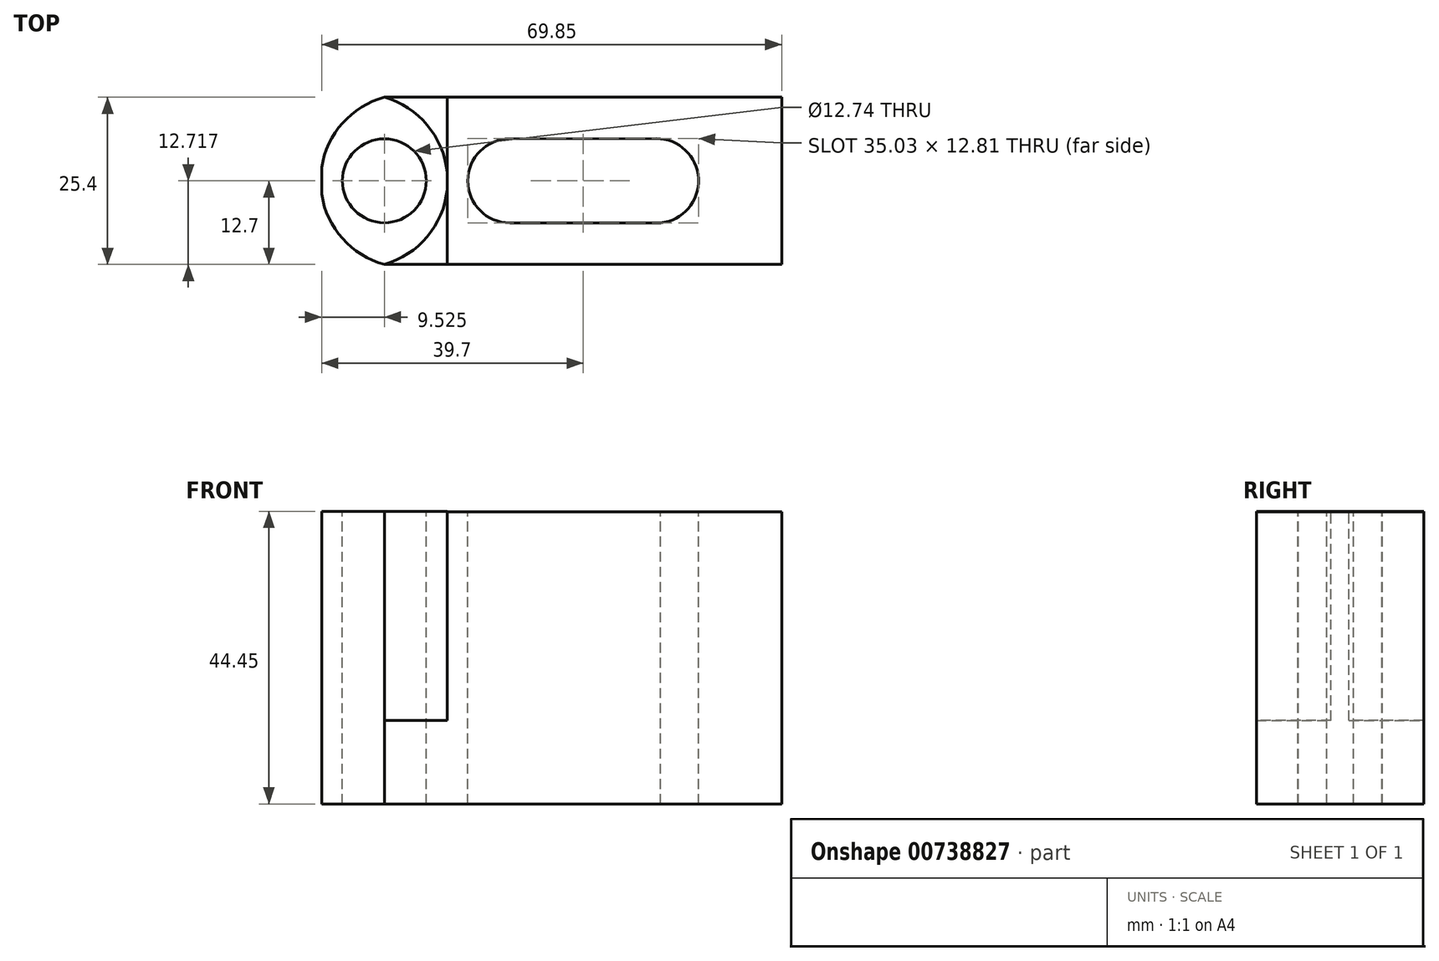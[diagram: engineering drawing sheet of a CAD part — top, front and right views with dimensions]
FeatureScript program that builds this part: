
annotation { "Feature Type Name" : "Feature", "Feature Type Description" : "" }
export const myFeature = defineFeature(function(context is Context, id is Id, definition is map)
    precondition{}
    {
        {
            var Q0;
            Q0=qCreatedBy(makeId("Front.planeOp"),FACE);
            var sketch = newSketch(context, id + "F0", { "sketchPlane" : qUnion([Q0])});
            skLineSegment(sketch, "E0", {"start": v(0, 0) * mm, "end": v(0, 44.45) * mm});
            skLineSegment(sketch, "E1", {"start": v(0, 44.45) * mm, "end": v(69.85, 44.45) * mm});
            skLineSegment(sketch, "E2", {"start": v(69.85, 44.45) * mm, "end": v(69.85, 0) * mm});
            skLineSegment(sketch, "E3", {"start": v(69.85, 0) * mm, "end": v(0, 0) * mm});
            skSolve(sketch);
        }
        {
            var Q0;
            Q0 = qSketchRegion(id + "F0", true);
            extrude(context, id + "F1", {"entities" : qUnion([Q0]), "depth" : 25.4 * mm, "offsetDistance" : 25.4 * mm});
        }
        {
            var Q0;
            Q0=makeQuery(id+"F1.opExtrude","SWEPT_FACE",FACE,{"disambiguationData":[OSD([sQuery(id+"F0.wireOp",EDGE,"E1")])]});
            var sketch = newSketch(context, id + "F2", { "sketchPlane" : qUnion([Q0])});
            skLineSegment(sketch, "E4", {"start": v(19.05, 0) * mm, "end": v(19.05, -25.4) * mm});
            skSolve(sketch);
        }
        {
            var Q0;
            {var subQ0=sQuery(id+"F2.wireOp",EDGE,"E4");Q0=makeQuery(id+"F2.imprint","IMPRINT",FACE,{"disambiguationData":[TD([[makeQuery(id+"F2.imprint","IMPRINT",EDGE,{"derivedFrom":subQ0}),1.0]])]});}
            extrude(context, id + "F3", {"entities" : qUnion([Q0]), "operationType" : NewBodyOperationType.REMOVE, "oppositeDirection" : true, "depth" : 5 / 101.6 * mm, "offsetDistance" : 25.4 * mm});
        }
        {
            var Q0;
            Q0=makeQuery(id+"F1.opExtrude","SWEPT_FACE",FACE,{"disambiguationData":[OSD([sQuery(id+"F0.wireOp",EDGE,"E1")])]});
            var sketch = newSketch(context, id + "F4", { "sketchPlane" : qUnion([Q0])});
            skLineSegment(sketch, "E5", {"start": v(9.53, 0) * mm, "end": v(9.53, -25.4) * mm});
            skCircle(sketch, "E6", {"center": v(9.53, -12.7) * mm, "radius": 6.37 * mm});
            skArc(sketch, "E7", {"start": v(9.53, -25.4) * mm, "mid": v(19.15, -12.7) * mm, "end": v(9.53, 0) * mm});
            skArc(sketch, "E8", {"start": v(9.53, 0) * mm, "mid": v(-0.16, -12.7) * mm, "end": v(9.53, -25.4) * mm});
            skSolve(sketch);
        }
        {
            var Q0;
            {var subQ0=sQuery(id+"F4.wireOp",EDGE,"E6");var subQ1=sQuery(id+"F4.wireOp",EDGE,"E5");var subQ2=makeQuery(id+"F4.imprint","INTERSECT",VERTEX,{"disambiguationData":[OD(0.0)],"derivedFrom":[subQ1,subQ0]});Q0=makeQuery(id+"F4.imprint","IMPRINT",FACE,{"disambiguationData":[TD([[makeQuery(id+"F4.imprint","IMPRINT",EDGE,{"disambiguationData":[TD([[subQ2,-1.0]])],"derivedFrom":subQ1}),-1.0]])]});}
            var Q1;
            {var subQ0=sQuery(id+"F4.wireOp",EDGE,"E6");var subQ1=sQuery(id+"F4.wireOp",EDGE,"E5");var subQ2=makeQuery(id+"F4.imprint","INTERSECT",VERTEX,{"disambiguationData":[OD(0.0)],"derivedFrom":[subQ1,subQ0]});Q1=makeQuery(id+"F4.imprint","IMPRINT",FACE,{"disambiguationData":[TD([[makeQuery(id+"F4.imprint","IMPRINT",EDGE,{"disambiguationData":[TD([[subQ2,-1.0]])],"derivedFrom":subQ1}),1.0]])]});}
            var Q2;
            {var subQ0=sQuery(id+"F4.wireOp",EDGE,"E8");var subQ1=sQuery(id+"F0.wireOp",EDGE,"E1");var subQ4=makeQuery(id+"F1.opExtrude","SWEPT_EDGE",EDGE,{"disambiguationData":[OSD([sQuery(id+"F0.wireOp",EDGE,"E0"),subQ1])]});var subQ5=makeQuery(id+"F4.imprint","INTERSECT",VERTEX,{"disambiguationData":[OD(0.0)],"derivedFrom":[subQ4,subQ0]});Q2=makeQuery(id+"F4.imprint","IMPRINT",FACE,{"disambiguationData":[TD([[makeQuery(id+"F4.imprint","IMPRINT",EDGE,{"disambiguationData":[TD([[subQ5,1.0]])],"derivedFrom":subQ0}),-1.0]])]});}
            var Q3;
            {var subQ0=sQuery(id+"F4.wireOp",EDGE,"E8");var subQ1=sQuery(id+"F0.wireOp",EDGE,"E1");var subQ4=makeQuery(id+"F1.opExtrude","SWEPT_EDGE",EDGE,{"disambiguationData":[OSD([sQuery(id+"F0.wireOp",EDGE,"E0"),subQ1])]});var subQ5=makeQuery(id+"F4.imprint","INTERSECT",VERTEX,{"disambiguationData":[OD(1.0)],"derivedFrom":[subQ4,subQ0]});Q3=makeQuery(id+"F4.imprint","IMPRINT",FACE,{"disambiguationData":[TD([[makeQuery(id+"F4.imprint","IMPRINT",EDGE,{"disambiguationData":[TD([[subQ5,-1.0]])],"derivedFrom":subQ0}),-1.0]])]});}
            extrude(context, id + "F5", {"entities" : qUnion([Q0, Q1, Q2, Q3]), "operationType" : NewBodyOperationType.REMOVE, "endBound" : BoundingType.THROUGH_ALL, "oppositeDirection" : true, "depth" : 25.4 * mm, "offsetDistance" : 25.4 * mm});
        }
        {
            var Q0;
            Q0=makeQuery(id+"F1.opExtrude","SWEPT_FACE",FACE,{"disambiguationData":[OSD([sQuery(id+"F0.wireOp",EDGE,"E1")])]});
            var sketch = newSketch(context, id + "F6", { "sketchPlane" : qUnion([Q0])});
            skArc(sketch, "E9", {"start": v(9.53, -25.4) * mm, "mid": v(19.12, -12.7) * mm, "end": v(9.53, 0) * mm});
            skSolve(sketch);
        }
        {
            var Q0;
            {var subQ1=sQuery(id+"F0.wireOp",EDGE,"E1");var subQ2=makeQuery(id+"F1.opExtrude","CAP_EDGE",EDGE,{"disambiguationData":[OSD([subQ1])],"isStart":true});var subQ3=subQ2;Q0=makeQuery(id+"F6.imprint","IMPRINT",FACE,{"disambiguationData":[TD([[makeQuery(id+"F6.imprint","IMPRINT",EDGE,{"derivedFrom":subQ3}),-1.0]])]});}
            var Q1;
            {var subQ1=sQuery(id+"F0.wireOp",EDGE,"E1");var subQ2=makeQuery(id+"F1.opExtrude","CAP_EDGE",EDGE,{"disambiguationData":[OSD([subQ1])],"isStart":false});var subQ3=subQ2;Q1=makeQuery(id+"F6.imprint","IMPRINT",FACE,{"disambiguationData":[TD([[makeQuery(id+"F6.imprint","IMPRINT",EDGE,{"derivedFrom":subQ3}),1.0]])]});}
            extrude(context, id + "F7", {"entities" : qUnion([Q0, Q1]), "operationType" : NewBodyOperationType.REMOVE, "oppositeDirection" : true, "depth" : 31.75 * mm, "offsetDistance" : 25.4 * mm});
        }
        {
            var Q0;
            {var subQ0=sQuery(id+"F0.wireOp",EDGE,"E1");var subQ1=makeQuery(id+"F1.opExtrude","CAP_EDGE",EDGE,{"disambiguationData":[OSD([subQ0])],"isStart":true});var subQ2=subQ1;var subQ3=sQuery(id+"F2.wireOp",EDGE,"E4");var subQ4=makeQuery(id+"F3.boolean.opBoolean","COPY",EDGE,{"derivedFrom":makeQuery(id+"F3.opExtrude","CAP_EDGE",EDGE,{"disambiguationData":[OSD([subQ3])],"isStart":true})});var subQ5=sQuery(id+"F6.wireOp",EDGE,"E9");var subQ6=makeQuery(id+"F6.imprint","INTERSECT",VERTEX,{"disambiguationData":[OD(1.0)],"derivedFrom":[subQ4,subQ5]});var subQ11=makeQuery(id+"F1.opExtrude","CAP_EDGE",EDGE,{"disambiguationData":[OSD([subQ0])],"isStart":false});var subQ12=subQ11;var subQ13=makeQuery(id+"F6.imprint","INTERSECT",VERTEX,{"disambiguationData":[OD(0.0)],"derivedFrom":[subQ4,subQ5]});Q0=makeQuery(id+"F7.boolean.opBoolean","MERGE",FACE,{"derivedFrom":[makeQuery(id+"F3.boolean.opBoolean","COPY",FACE,{"derivedFrom":makeQuery(id+"F3.opExtrude","CAP_FACE",FACE,{"disambiguationData":[OSD([subQ0,sQuery(id+"F0.wireOp",EDGE,"E2"),subQ3])],"isStart":false})}),makeQuery(id+"F7.opExtrude","CAP_FACE",FACE,{"disambiguationData":[OSD([subQ0,subQ3,subQ5]),TDD([makeQuery(id+"F6.imprint","IMPRINT",EDGE,{"disambiguationData":[TD([[subQ13,1.0]])],"derivedFrom":subQ5}),makeQuery(id+"F6.imprint","IMPRINT",EDGE,{"derivedFrom":subQ12}),makeQuery(id+"F6.imprint","IMPRINT",EDGE,{"disambiguationData":[TD([[makeQuery(id+"F6.imprint","INTERSECT",VERTEX,{"derivedFrom":[subQ4,subQ12]}),1.0]])],"derivedFrom":subQ4})])],"isStart":false}),makeQuery(id+"F7.opExtrude","CAP_FACE",FACE,{"disambiguationData":[OSD([subQ0,subQ3,subQ5]),TDD([makeQuery(id+"F6.imprint","IMPRINT",EDGE,{"disambiguationData":[TD([[subQ6,-1.0]])],"derivedFrom":subQ5}),makeQuery(id+"F6.imprint","IMPRINT",EDGE,{"derivedFrom":subQ2}),makeQuery(id+"F6.imprint","IMPRINT",EDGE,{"disambiguationData":[TD([[makeQuery(id+"F6.imprint","INTERSECT",VERTEX,{"derivedFrom":[subQ4,subQ2]}),-1.0]])],"derivedFrom":subQ4})])],"isStart":false})]});}
            var sketch = newSketch(context, id + "F8", { "sketchPlane" : qUnion([Q0])});
            skLineSegment(sketch, "E10", {"start": v(28.58, 0) * mm, "end": v(28.58, -25.4) * mm});
            skLineSegment(sketch, "E11", {"start": v(50.8, 0) * mm, "end": v(50.8, -25.4) * mm});
            skLineSegment(sketch, "E12", {"start": v(28.58, -12.7) * mm, "end": v(50.8, -12.7) * mm});
            skCircle(sketch, "E13", {"center": v(28.58, -12.7) * mm, "radius": 6.39 * mm});
            skCircle(sketch, "E14", {"center": v(50.8, -12.7) * mm, "radius": 6.42 * mm});
            skLineSegment(sketch, "E15", {"start": v(28.58, -6.31) * mm, "end": v(50.8, -6.28) * mm});
            skLineSegment(sketch, "E16", {"start": v(28.58, -19.09) * mm, "end": v(51.47, -19.09) * mm});
            skArc(sketch, "E17", {"start": v(50.8, -25.4) * mm, "mid": v(69.82, -12.7) * mm, "end": v(50.8, 0) * mm});
            skSolve(sketch);
        }
        {
            var Q0;
            {var subQ0=sQuery(id+"F8.wireOp",EDGE,"E10");var subQ1=makeQuery(id+"F8.imprint","INTERSECT",VERTEX,{"derivedFrom":[subQ0,sQuery(id+"F8.wireOp",EDGE,"E12")]});Q0=makeQuery(id+"F8.imprint","IMPRINT",FACE,{"disambiguationData":[TD([[makeQuery(id+"F8.imprint","IMPRINT",EDGE,{"disambiguationData":[TD([[subQ1,1.0]])],"derivedFrom":subQ0}),-1.0]])]});}
            var Q1;
            {var subQ0=sQuery(id+"F8.wireOp",EDGE,"E12");var subQ1=sQuery(id+"F8.wireOp",EDGE,"E10");var subQ2=makeQuery(id+"F8.imprint","INTERSECT",VERTEX,{"derivedFrom":[subQ1,subQ0]});Q1=makeQuery(id+"F8.imprint","IMPRINT",FACE,{"disambiguationData":[TD([[makeQuery(id+"F8.imprint","IMPRINT",EDGE,{"disambiguationData":[TD([[subQ2,-1.0]])],"derivedFrom":subQ0}),1.0]])]});}
            var Q2;
            {var subQ0=sQuery(id+"F8.wireOp",EDGE,"E12");var subQ1=sQuery(id+"F8.wireOp",EDGE,"E10");var subQ2=makeQuery(id+"F8.imprint","INTERSECT",VERTEX,{"derivedFrom":[subQ1,subQ0]});Q2=makeQuery(id+"F8.imprint","IMPRINT",FACE,{"disambiguationData":[TD([[makeQuery(id+"F8.imprint","IMPRINT",EDGE,{"disambiguationData":[TD([[subQ2,-1.0]])],"derivedFrom":subQ0}),-1.0]])]});}
            var Q3;
            {var subQ5=sQuery(id+"F8.wireOp",EDGE,"E15");Q3=makeQuery(id+"F8.imprint","IMPRINT",FACE,{"disambiguationData":[TD([[makeQuery(id+"F8.imprint","IMPRINT",EDGE,{"derivedFrom":subQ5}),-1.0]])]});}
            var Q4;
            {var subQ0=sQuery(id+"F8.wireOp",EDGE,"E13");var subQ1=sQuery(id+"F8.wireOp",EDGE,"E12");var subQ2=makeQuery(id+"F8.imprint","INTERSECT",VERTEX,{"derivedFrom":[subQ1,subQ0]});Q4=makeQuery(id+"F8.imprint","IMPRINT",FACE,{"disambiguationData":[TD([[makeQuery(id+"F8.imprint","IMPRINT",EDGE,{"disambiguationData":[TD([[subQ2,-1.0]])],"derivedFrom":subQ1}),-1.0]])]});}
            var Q5;
            {var subQ0=sQuery(id+"F8.wireOp",EDGE,"E12");var subQ1=sQuery(id+"F8.wireOp",EDGE,"E11");var subQ2=makeQuery(id+"F8.imprint","INTERSECT",VERTEX,{"derivedFrom":[subQ1,subQ0]});Q5=makeQuery(id+"F8.imprint","IMPRINT",FACE,{"disambiguationData":[TD([[makeQuery(id+"F8.imprint","IMPRINT",EDGE,{"disambiguationData":[TD([[subQ2,-1.0]])],"derivedFrom":subQ1}),-1.0]])]});}
            var Q6;
            {var subQ0=sQuery(id+"F8.wireOp",EDGE,"E12");var subQ1=sQuery(id+"F8.wireOp",EDGE,"E11");var subQ2=makeQuery(id+"F8.imprint","INTERSECT",VERTEX,{"derivedFrom":[subQ1,subQ0]});Q6=makeQuery(id+"F8.imprint","IMPRINT",FACE,{"disambiguationData":[TD([[makeQuery(id+"F8.imprint","IMPRINT",EDGE,{"disambiguationData":[TD([[subQ2,1.0]])],"derivedFrom":subQ1}),-1.0]])]});}
            var Q7;
            {var subQ0=sQuery(id+"F8.wireOp",EDGE,"E11");var subQ1=makeQuery(id+"F8.imprint","INTERSECT",VERTEX,{"derivedFrom":[subQ0,sQuery(id+"F8.wireOp",EDGE,"E12")]});Q7=makeQuery(id+"F8.imprint","IMPRINT",FACE,{"disambiguationData":[TD([[makeQuery(id+"F8.imprint","IMPRINT",EDGE,{"disambiguationData":[TD([[subQ1,1.0]])],"derivedFrom":subQ0}),1.0]])]});}
            var Q8;
            {var subQ1=sQuery(id+"F0.wireOp",EDGE,"E1");var subQ3=sQuery(id+"F0.wireOp",EDGE,"E2");var subQ11=makeQuery(id+"F3.boolean.opBoolean","COPY",EDGE,{"derivedFrom":makeQuery(id+"F3.opExtrude","CAP_EDGE",EDGE,{"disambiguationData":[OSD([subQ1,subQ3])],"isStart":false})});Q8=makeQuery(id+"F8.imprint","IMPRINT",FACE,{"disambiguationData":[TD([[makeQuery(id+"F8.imprint","IMPRINT",EDGE,{"derivedFrom":subQ11}),1.0]])]});}
            extrude(context, id + "F9", {"entities" : qUnion([Q0, Q1, Q2, Q3, Q4, Q5, Q6, Q7, Q8]), "operationType" : NewBodyOperationType.REMOVE, "endBound" : BoundingType.THROUGH_ALL, "oppositeDirection" : true, "depth" : 25.4 * mm, "offsetDistance" : 25.4 * mm});
        }
    });
